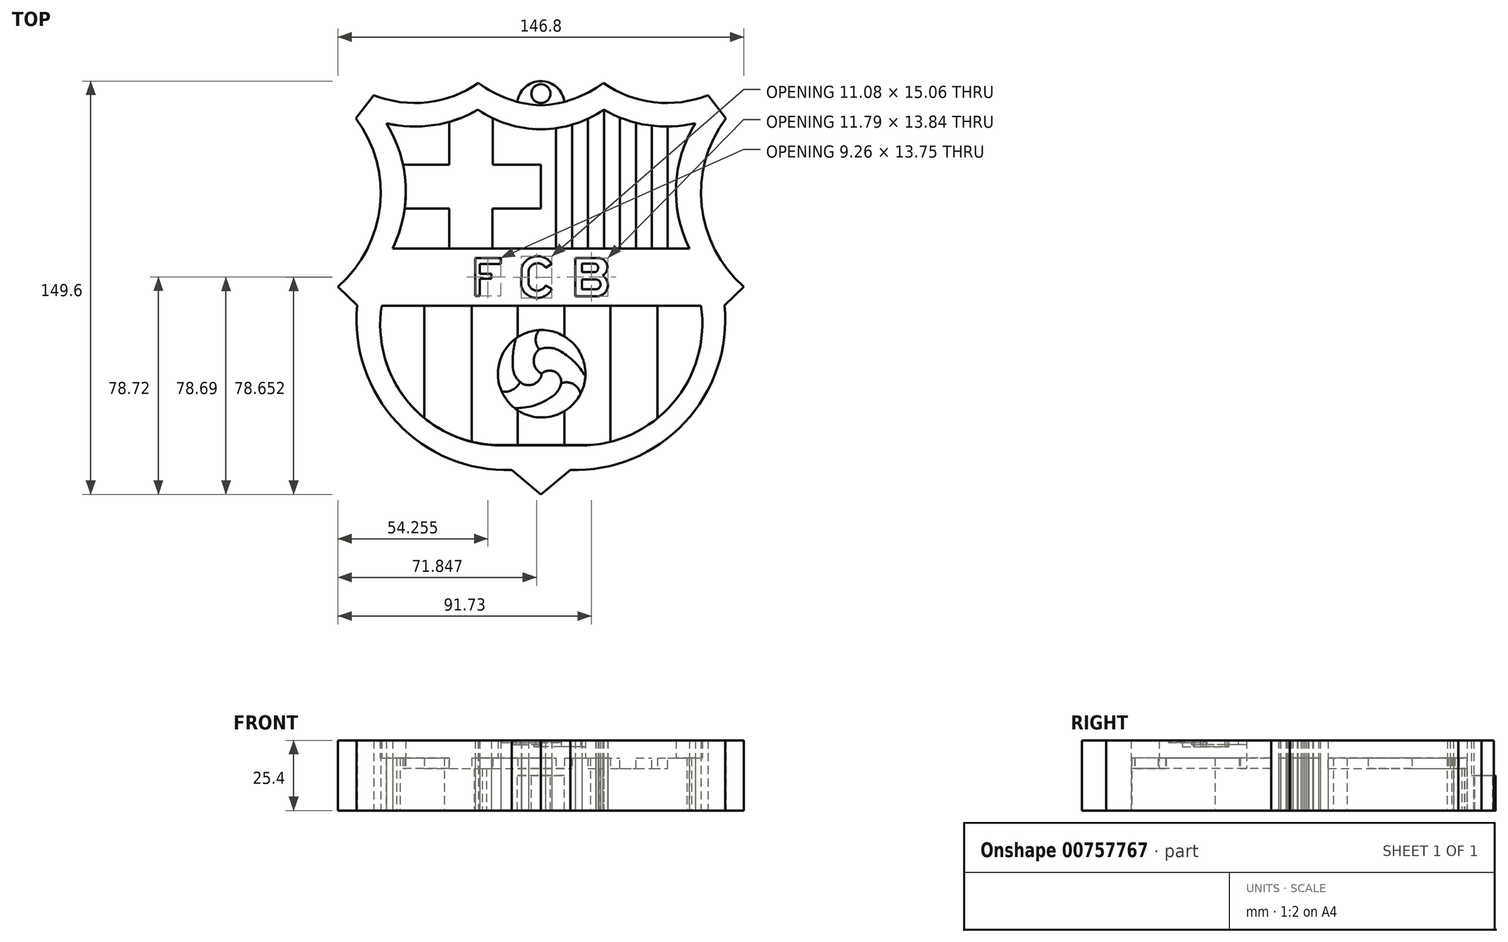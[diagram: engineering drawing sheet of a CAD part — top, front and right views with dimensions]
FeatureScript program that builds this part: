
annotation { "Feature Type Name" : "Feature", "Feature Type Description" : "" }
export const myFeature = defineFeature(function(context is Context, id is Id, definition is map)
    precondition{}
    {
        {
            var Q0;
            Q0=qCreatedBy(makeId("Top.planeOp"),FACE);
            var sketch = newSketch(context, id + "F0", { "sketchPlane" : qUnion([Q0])});
            skPoint(sketch, "E0", {"position": v(-76.27, 79.4) * mm});
            skPoint(sketch, "E1", {"position": v(76.57, -75.74) * mm});
            skLineSegment(sketch, "E2", {"start": v(-60.43, 71.38) * mm, "end": v(-66.94, 63.03) * mm});
            skLineSegment(sketch, "E3", {"start": v(-66.45, -4.73) * mm, "end": v(-73.4, 2.08) * mm});
            skArc(sketch, "E4", {"start": v(-73.4, 2.08) * mm, "mid": v(-58.2, 31.29) * mm, "end": v(-66.94, 63.03) * mm});
            skLineSegment(sketch, "E5", {"start": v(0, -73.13) * mm, "end": v(-10.6, -64.3) * mm});
            skArc(sketch, "E6", {"start": v(-66.45, -4.73) * mm, "mid": v(-51.99, -47.14) * mm, "end": v(-10.6, -64.3) * mm});
            skArc(sketch, "E7", {"start": v(-60.43, 71.38) * mm, "mid": v(-40.97, 68.83) * mm, "end": v(-22.62, 75.8) * mm});
            skArc(sketch, "E8", {"start": v(-22.62, 75.8) * mm, "mid": v(-11.9, 70.06) * mm, "end": v(0, 67.68) * mm});
            skLineSegment(sketch, "E9", {"start": v(0, 0) * mm, "end": v(0, 20) * mm, "construction": true});
            skArc(sketch, "E10.MirrorCS", {"start": v(22.62, 75.8) * mm, "mid": v(11.9, 70.06) * mm, "end": v(0, 67.68) * mm});
            skArc(sketch, "E11.MirrorCS", {"start": v(60.43, 71.38) * mm, "mid": v(40.97, 68.83) * mm, "end": v(22.62, 75.8) * mm});
            skLineSegment(sketch, "E12.MirrorCS", {"start": v(60.43, 71.38) * mm, "end": v(66.94, 63.03) * mm});
            skArc(sketch, "E13.MirrorCS", {"start": v(73.4, 2.08) * mm, "mid": v(58.2, 31.29) * mm, "end": v(66.94, 63.03) * mm});
            skLineSegment(sketch, "E14.MirrorCS", {"start": v(66.45, -4.73) * mm, "end": v(73.4, 2.08) * mm});
            skArc(sketch, "E15.MirrorCS", {"start": v(66.45, -4.73) * mm, "mid": v(51.99, -47.14) * mm, "end": v(10.6, -64.3) * mm});
            skLineSegment(sketch, "E16.MirrorCS", {"start": v(0, -73.13) * mm, "end": v(10.6, -64.3) * mm});
            skLineSegment(sketch, "E17", {"start": v(-53.66, 15.92) * mm, "end": v(0, 15.92) * mm});
            skLineSegment(sketch, "E18", {"start": v(0, 15.92) * mm, "end": v(0, 59.07) * mm});
            skArc(sketch, "E19", {"start": v(-22.73, 66.12) * mm, "mid": v(-11.89, 60.9) * mm, "end": v(0, 59.07) * mm});
            skArc(sketch, "E20", {"start": v(-55.86, 61.22) * mm, "mid": v(-38.83, 60.53) * mm, "end": v(-22.73, 66.12) * mm});
            skArc(sketch, "E21", {"start": v(-53.66, 15.92) * mm, "mid": v(-48.93, 38.85) * mm, "end": v(-55.86, 61.22) * mm});
            skLineSegment(sketch, "E22", {"start": v(0, 15.92) * mm, "end": v(53.66, 15.92) * mm});
            skArc(sketch, "E23.MirrorCS", {"start": v(22.73, 66.12) * mm, "mid": v(11.89, 60.9) * mm, "end": v(0, 59.07) * mm});
            skArc(sketch, "E24.MirrorCS", {"start": v(55.86, 61.22) * mm, "mid": v(38.83, 60.53) * mm, "end": v(22.73, 66.12) * mm});
            skArc(sketch, "E25.MirrorCS", {"start": v(53.66, 15.92) * mm, "mid": v(48.93, 38.85) * mm, "end": v(55.86, 61.22) * mm});
            skLineSegment(sketch, "E26", {"start": v(57.9, -4.76) * mm, "end": v(-57.54, -4.76) * mm});
            skCircle(sketch, "E27", {"center": v(0.28, -29.44) * mm, "radius": 15.83 * mm});
            skLineSegment(sketch, "E28", {"start": v(-14.52, -55.39) * mm, "end": v(14.4, -55.39) * mm});
            skArc(sketch, "E29", {"start": v(-57.54, -4.76) * mm, "mid": v(-47.74, -40.02) * mm, "end": v(-14.52, -55.39) * mm});
            skArc(sketch, "E30", {"start": v(14.4, -55.39) * mm, "mid": v(47.77, -40.06) * mm, "end": v(57.9, -4.76) * mm});
            skArc(sketch, "E31", {"start": v(-7.51, -32.42) * mm, "mid": v(-2.72, -33.27) * mm, "end": v(0.28, -29.44) * mm});
            skArc(sketch, "E32", {"start": v(-14.15, -35.94) * mm, "mid": v(-10.27, -35.25) * mm, "end": v(-7.51, -32.42) * mm});
            skArc(sketch, "E33", {"start": v(7.38, -32.9) * mm, "mid": v(5.02, -28.72) * mm, "end": v(0.28, -29.44) * mm});
            skArc(sketch, "E34", {"start": v(14.31, -36.77) * mm, "mid": v(11.75, -33.2) * mm, "end": v(7.38, -32.9) * mm});
            skArc(sketch, "E35", {"start": v(-0.6, -20.63) * mm, "mid": v(-2.57, -25.28) * mm, "end": v(0.28, -29.44) * mm});
            skArc(sketch, "E36", {"start": v(-0.6, -13.64) * mm, "mid": v(-1.92, -17.14) * mm, "end": v(-0.6, -20.63) * mm});
            skArc(sketch, "E37", {"start": v(-10.04, -27.9) * mm, "mid": v(-9.2, -30.4) * mm, "end": v(-7.51, -32.42) * mm});
            skArc(sketch, "E38", {"start": v(-9.08, -16.68) * mm, "mid": v(-10.07, -22.25) * mm, "end": v(-10.04, -27.9) * mm});
            skArc(sketch, "E39", {"start": v(3.53, -38.02) * mm, "mid": v(6, -35.87) * mm, "end": v(7.38, -32.9) * mm});
            skArc(sketch, "E40", {"start": v(-9.55, -41.84) * mm, "mid": v(-2.7, -41) * mm, "end": v(3.53, -38.02) * mm});
            skArc(sketch, "E41", {"start": v(7.38, -21.5) * mm, "mid": v(3.5, -20.07) * mm, "end": v(-0.6, -20.63) * mm});
            skArc(sketch, "E42", {"start": v(16.09, -30.2) * mm, "mid": v(12.26, -25.33) * mm, "end": v(7.38, -21.5) * mm});
            skLineSegment(sketch, "E43", {"start": v(-23.7, 12.46) * mm, "end": v(-14.52, 12.46) * mm});
            skLineSegment(sketch, "E44", {"start": v(-14.52, 12.46) * mm, "end": v(-14.52, 10.23) * mm});
            skLineSegment(sketch, "E45", {"start": v(-14.52, 10.23) * mm, "end": v(-22.05, 10.23) * mm});
            skLineSegment(sketch, "E46", {"start": v(-22.05, 10.23) * mm, "end": v(-22.05, 6.7) * mm});
            skLineSegment(sketch, "E47", {"start": v(-22.05, 6.7) * mm, "end": v(-17.95, 6.7) * mm});
            skLineSegment(sketch, "E48", {"start": v(-17.95, 6.7) * mm, "end": v(-17.95, 4.93) * mm});
            skLineSegment(sketch, "E49", {"start": v(-17.95, 4.93) * mm, "end": v(-22.05, 4.93) * mm});
            skLineSegment(sketch, "E50", {"start": v(-22.05, 4.93) * mm, "end": v(-22.05, -1.28) * mm});
            skLineSegment(sketch, "E51", {"start": v(-22.05, -1.28) * mm, "end": v(-23.77, -1.28) * mm});
            skLineSegment(sketch, "E52", {"start": v(-23.77, -1.28) * mm, "end": v(-23.7, 12.46) * mm});
            skArc(sketch, "E53", {"start": v(-4.47, 3.16) * mm, "mid": v(-1.6, 0.65) * mm, "end": v(1.71, 2.57) * mm});
            skArc(sketch, "E54", {"start": v(1.66, 8.95) * mm, "mid": v(-1.7, 10.52) * mm, "end": v(-4.42, 8.01) * mm});
            skArc(sketch, "E55", {"start": v(3.99, 10.24) * mm, "mid": v(-2.05, 13.05) * mm, "end": v(-7.05, 8.66) * mm});
            skArc(sketch, "E56", {"start": v(-7.1, 2.27) * mm, "mid": v(-1.88, -2) * mm, "end": v(3.99, 1.33) * mm});
            skLineSegment(sketch, "E57", {"start": v(1.66, 8.95) * mm, "end": v(3.99, 10.24) * mm});
            skLineSegment(sketch, "E58", {"start": v(1.71, 2.57) * mm, "end": v(3.99, 1.33) * mm});
            skLineSegment(sketch, "E59", {"start": v(-4.47, 3.16) * mm, "end": v(-4.42, 8.01) * mm});
            skLineSegment(sketch, "E60", {"start": v(-7.05, 8.66) * mm, "end": v(-7.1, 2.27) * mm});
            skLineSegment(sketch, "E61", {"start": v(12.43, 12.48) * mm, "end": v(12.43, -1.36) * mm});
            skLineSegment(sketch, "E62", {"start": v(12.43, -1.36) * mm, "end": v(21, -1.36) * mm});
            skLineSegment(sketch, "E63", {"start": v(12.43, 12.48) * mm, "end": v(20.7, 12.48) * mm});
            skArc(sketch, "E64", {"start": v(22.34, 6.14) * mm, "mid": v(23.97, 9.95) * mm, "end": v(20.7, 12.48) * mm});
            skArc(sketch, "E65", {"start": v(21, -1.36) * mm, "mid": v(24.2, 1.94) * mm, "end": v(22.34, 6.14) * mm});
            skLineSegment(sketch, "E66", {"start": v(14.89, 10.38) * mm, "end": v(14.89, 7.4) * mm});
            skLineSegment(sketch, "E67", {"start": v(14.89, 7.4) * mm, "end": v(19.89, 7.4) * mm});
            skLineSegment(sketch, "E68", {"start": v(14.89, 10.38) * mm, "end": v(19.8, 10.38) * mm});
            skArc(sketch, "E69", {"start": v(19.89, 7.4) * mm, "mid": v(20.7, 8.91) * mm, "end": v(19.8, 10.38) * mm});
            skLineSegment(sketch, "E70", {"start": v(14.89, 4.67) * mm, "end": v(14.89, 1.14) * mm});
            skLineSegment(sketch, "E71", {"start": v(14.89, 1.14) * mm, "end": v(19.98, 1.14) * mm});
            skLineSegment(sketch, "E72", {"start": v(14.89, 4.67) * mm, "end": v(19.84, 4.67) * mm});
            skArc(sketch, "E73", {"start": v(19.98, 1.14) * mm, "mid": v(21.6, 2.97) * mm, "end": v(19.84, 4.67) * mm});
            skLineSegment(sketch, "E74", {"start": v(0, 59.07) * mm, "end": v(0, 15.92) * mm});
            skSolve(sketch);
        }
        {
            var Q0;
            Q0=makeQuery(id+"F0.imprint","IMPRINT",FACE,{"disambiguationData":[TD([[makeQuery(id+"F0.imprint","IMPRINT",EDGE,{"derivedFrom":sQuery(id+"F0.wireOp",EDGE,"E2")}),1.0]])]});
            var Q1;
            Q1=makeQuery(id+"F0.imprint","IMPRINT",FACE,{"disambiguationData":[TD([[makeQuery(id+"F0.imprint","IMPRINT",EDGE,{"derivedFrom":sQuery(id+"F0.wireOp",EDGE,"E70")}),1.0]])]});
            var Q2;
            Q2=makeQuery(id+"F0.imprint","IMPRINT",FACE,{"disambiguationData":[TD([[makeQuery(id+"F0.imprint","IMPRINT",EDGE,{"derivedFrom":sQuery(id+"F0.wireOp",EDGE,"E66")}),1.0]])]});
            extrude(context, id + "F1", {"entities" : qUnion([Q0, Q1, Q2]), "depth" : 25.4 * mm, "offsetDistance" : 25.4 * mm});
        }
        {
            var Q0;
            Q0=qCreatedBy(makeId("Top.planeOp"),FACE);
            var sketch = newSketch(context, id + "F2", { "sketchPlane" : qUnion([Q0])});
            skLineSegment(sketch, "E75", {"start": v(0, 59.08) * mm, "end": v(0, 15.9) * mm});
            skLineSegment(sketch, "E76", {"start": v(0, 15.9) * mm, "end": v(-53.6, 15.9) * mm});
            skLineSegment(sketch, "E77", {"start": v(-53.6, 15.9) * mm, "end": v(53.65, 15.9) * mm});
            skLineSegment(sketch, "E78", {"start": v(-33.18, 15.9) * mm, "end": v(-33.18, 30.4) * mm});
            skLineSegment(sketch, "E79", {"start": v(-33.18, 30.4) * mm, "end": v(-49.25, 30.4) * mm});
            skLineSegment(sketch, "E80", {"start": v(-17.48, 15.9) * mm, "end": v(-17.48, 30.4) * mm});
            skLineSegment(sketch, "E81", {"start": v(-17.48, 30.4) * mm, "end": v(0, 30.4) * mm});
            skLineSegment(sketch, "E82", {"start": v(-17.47, 46.21) * mm, "end": v(0, 46.21) * mm});
            skLineSegment(sketch, "E83", {"start": v(-17.47, 46.21) * mm, "end": v(-17.47, 63.13) * mm});
            skLineSegment(sketch, "E84", {"start": v(-33.09, 46.2) * mm, "end": v(-33.09, 61.74) * mm});
            skLineSegment(sketch, "E85", {"start": v(-33.09, 46.2) * mm, "end": v(-49.97, 46.2) * mm});
            skArc(sketch, "E86", {"start": v(-49.25, 30.4) * mm, "mid": v(-48.9, 38.33) * mm, "end": v(-49.97, 46.2) * mm});
            skArc(sketch, "E87", {"start": v(-33.09, 61.74) * mm, "mid": v(-27.75, 63.57) * mm, "end": v(-22.75, 66.16) * mm});
            skArc(sketch, "E88", {"start": v(-22.75, 66.16) * mm, "mid": v(-20.18, 64.52) * mm, "end": v(-17.47, 63.13) * mm});
            skLineSegment(sketch, "E89", {"start": v(0, 15.9) * mm, "end": v(0, 59.08) * mm});
            skArc(sketch, "E90", {"start": v(55.86, 61.24) * mm, "mid": v(48.96, 38.85) * mm, "end": v(53.65, 15.9) * mm});
            skArc(sketch, "E91", {"start": v(22.75, 66.11) * mm, "mid": v(38.85, 60.6) * mm, "end": v(55.86, 61.24) * mm});
            skArc(sketch, "E92", {"start": v(0, 59.08) * mm, "mid": v(11.88, 60.97) * mm, "end": v(22.75, 66.11) * mm});
            skLineSegment(sketch, "E93", {"start": v(5.48, 15.9) * mm, "end": v(5.48, 59.52) * mm});
            skLineSegment(sketch, "E94", {"start": v(11.3, 15.9) * mm, "end": v(11.3, 60.8) * mm});
            skLineSegment(sketch, "E95", {"start": v(17, 15.9) * mm, "end": v(17, 62.93) * mm});
            skLineSegment(sketch, "E96", {"start": v(22.82, 15.9) * mm, "end": v(22.82, 66.07) * mm});
            skLineSegment(sketch, "E97", {"start": v(28.62, 15.9) * mm, "end": v(28.62, 63.32) * mm});
            skLineSegment(sketch, "E98", {"start": v(34.35, 15.9) * mm, "end": v(34.35, 61.48) * mm});
            skLineSegment(sketch, "E99", {"start": v(40.13, 15.9) * mm, "end": v(40.13, 60.42) * mm});
            skLineSegment(sketch, "E100", {"start": v(45.9, 15.9) * mm, "end": v(45.9, 60.1) * mm});
            skLineSegment(sketch, "E101", {"start": v(-57.54, -4.76) * mm, "end": v(57.91, -4.76) * mm});
            skLineSegment(sketch, "E102", {"start": v(-42.21, -4.76) * mm, "end": v(-42.21, -45.42) * mm});
            skLineSegment(sketch, "E103", {"start": v(-25.03, -4.76) * mm, "end": v(-25.03, -54.02) * mm});
            skLineSegment(sketch, "E104", {"start": v(-8.43, -4.76) * mm, "end": v(-8.43, -55.18) * mm});
            skLineSegment(sketch, "E105", {"start": v(8.52, -4.76) * mm, "end": v(8.52, -55.22) * mm});
            skLineSegment(sketch, "E106", {"start": v(25.2, -4.76) * mm, "end": v(25.2, -54.09) * mm});
            skLineSegment(sketch, "E107", {"start": v(42.14, -4.76) * mm, "end": v(42.14, -45.59) * mm});
            skArc(sketch, "E108", {"start": v(-57.54, -4.76) * mm, "mid": v(-48.81, -38.68) * mm, "end": v(-17.9, -55.16) * mm});
            skArc(sketch, "E109", {"start": v(18.4, -55.25) * mm, "mid": v(49.07, -38.54) * mm, "end": v(57.91, -4.76) * mm});
            skLineSegment(sketch, "E110", {"start": v(-17.9, -55.16) * mm, "end": v(18.4, -55.25) * mm});
            skArc(sketch, "E111", {"start": v(-53.6, 15.9) * mm, "mid": v(-48.99, 38.82) * mm, "end": v(-55.83, 61.17) * mm});
            skArc(sketch, "E112", {"start": v(-55.83, 61.17) * mm, "mid": v(-44.43, 60.1) * mm, "end": v(-33.09, 61.74) * mm});
            skArc(sketch, "E113", {"start": v(-17.47, 63.13) * mm, "mid": v(-8.95, 60.16) * mm, "end": v(0, 59.08) * mm});
            skSolve(sketch);
        }
        {
            var Q0;
            {var subQ0=sQuery(id+"F2.wireOp",EDGE,"E84");Q0=makeQuery(id+"F2.imprint","IMPRINT",FACE,{"disambiguationData":[TD([[makeQuery(id+"F2.imprint","IMPRINT",EDGE,{"derivedFrom":subQ0}),1.0]])]});}
            var Q1;
            {var subQ0=sQuery(id+"F2.wireOp",EDGE,"E82");Q1=makeQuery(id+"F2.imprint","IMPRINT",FACE,{"disambiguationData":[TD([[makeQuery(id+"F2.imprint","IMPRINT",EDGE,{"derivedFrom":subQ0}),1.0]])]});}
            var Q2;
            {var subQ0=sQuery(id+"F2.wireOp",EDGE,"E80");Q2=makeQuery(id+"F2.imprint","IMPRINT",FACE,{"disambiguationData":[TD([[makeQuery(id+"F2.imprint","IMPRINT",EDGE,{"derivedFrom":subQ0}),-1.0]])]});}
            var Q3;
            {var subQ4=sQuery(id+"F2.wireOp",EDGE,"E78");Q3=makeQuery(id+"F2.imprint","IMPRINT",FACE,{"disambiguationData":[TD([[makeQuery(id+"F2.imprint","IMPRINT",EDGE,{"derivedFrom":subQ4}),1.0]])]});}
            var Q4;
            {var subQ3=sQuery(id+"F2.wireOp",EDGE,"E102");Q4=makeQuery(id+"F2.imprint","IMPRINT",FACE,{"disambiguationData":[TD([[makeQuery(id+"F2.imprint","IMPRINT",EDGE,{"derivedFrom":subQ3}),-1.0]])]});}
            var Q5;
            {var subQ1=sQuery(id+"F2.wireOp",EDGE,"E103");Q5=makeQuery(id+"F2.imprint","IMPRINT",FACE,{"disambiguationData":[TD([[makeQuery(id+"F2.imprint","IMPRINT",EDGE,{"derivedFrom":subQ1}),1.0]])]});}
            var Q6;
            {var subQ4=sQuery(id+"F2.wireOp",EDGE,"E105");Q6=makeQuery(id+"F2.imprint","IMPRINT",FACE,{"disambiguationData":[TD([[makeQuery(id+"F2.imprint","IMPRINT",EDGE,{"derivedFrom":subQ4}),1.0]])]});}
            var Q7;
            {var subQ3=sQuery(id+"F2.wireOp",EDGE,"E107");Q7=makeQuery(id+"F2.imprint","IMPRINT",FACE,{"disambiguationData":[TD([[makeQuery(id+"F2.imprint","IMPRINT",EDGE,{"derivedFrom":subQ3}),1.0]])]});}
            var Q8;
            {var subQ0=sQuery(id+"F2.wireOp",EDGE,"E90");Q8=makeQuery(id+"F2.imprint","IMPRINT",FACE,{"disambiguationData":[TD([[makeQuery(id+"F2.imprint","IMPRINT",EDGE,{"derivedFrom":subQ0}),-1.0]])]});}
            var Q9;
            {var subQ0=sQuery(id+"F2.wireOp",EDGE,"E98");Q9=makeQuery(id+"F2.imprint","IMPRINT",FACE,{"disambiguationData":[TD([[makeQuery(id+"F2.imprint","IMPRINT",EDGE,{"derivedFrom":subQ0}),-1.0]])]});}
            var Q10;
            {var subQ0=sQuery(id+"F2.wireOp",EDGE,"E96");Q10=makeQuery(id+"F2.imprint","IMPRINT",FACE,{"disambiguationData":[TD([[makeQuery(id+"F2.imprint","IMPRINT",EDGE,{"derivedFrom":subQ0}),-1.0]])]});}
            var Q11;
            {var subQ0=sQuery(id+"F2.wireOp",EDGE,"E94");Q11=makeQuery(id+"F2.imprint","IMPRINT",FACE,{"disambiguationData":[TD([[makeQuery(id+"F2.imprint","IMPRINT",EDGE,{"derivedFrom":subQ0}),-1.0]])]});}
            var Q12;
            {var subQ7=sQuery(id+"F2.wireOp",EDGE,"E93");Q12=makeQuery(id+"F2.imprint","IMPRINT",FACE,{"disambiguationData":[TD([[makeQuery(id+"F2.imprint","IMPRINT",EDGE,{"derivedFrom":subQ7}),1.0]])]});}
            extrude(context, id + "F3", {"entities" : qUnion([Q0, Q1, Q2, Q3, Q4, Q5, Q6, Q7, Q8, Q9, Q10, Q11, Q12]), "operationType" : NewBodyOperationType.ADD, "depth" : 19.05 * mm, "offsetDistance" : 25.4 * mm});
        }
        {
            var Q0;
            Q0 = qSketchRegion(id + "F0", true);
            var Q1;
            {var subQ0=sQuery(id+"F0.wireOp",EDGE,"E36");Q1=makeQuery(id+"F0.imprint","IMPRINT",FACE,{"disambiguationData":[TD([[makeQuery(id+"F0.imprint","IMPRINT",EDGE,{"derivedFrom":subQ0}),1.0]])]});}
            var Q2;
            {var subQ0=sQuery(id+"F0.wireOp",EDGE,"E34");Q2=makeQuery(id+"F0.imprint","IMPRINT",FACE,{"disambiguationData":[TD([[makeQuery(id+"F0.imprint","IMPRINT",EDGE,{"derivedFrom":subQ0}),1.0]])]});}
            var Q3;
            {var subQ0=sQuery(id+"F0.wireOp",EDGE,"E32");Q3=makeQuery(id+"F0.imprint","IMPRINT",FACE,{"disambiguationData":[TD([[makeQuery(id+"F0.imprint","IMPRINT",EDGE,{"derivedFrom":subQ0}),1.0]])]});}
            extrude(context, id + "F4", {"entities" : qUnion([Q0, Q1, Q2, Q3]), "operationType" : NewBodyOperationType.ADD, "depth" : 25.4 * mm, "offsetDistance" : 25.4 * mm});
        }
        {
            var Q0;
            Q0=makeQuery(id+"F0.imprint","IMPRINT",FACE,{"disambiguationData":[TD([[makeQuery(id+"F0.imprint","IMPRINT",EDGE,{"derivedFrom":sQuery(id+"F0.wireOp",EDGE,"E31")}),1.0]])]});
            extrude(context, id + "F5", {"entities" : qUnion([Q0]), "operationType" : NewBodyOperationType.ADD, "depth" : 23.88 * mm, "offsetDistance" : 25.4 * mm});
        }
        {
            var Q0;
            Q0=makeQuery(id+"F0.imprint","IMPRINT",FACE,{"disambiguationData":[TD([[makeQuery(id+"F0.imprint","IMPRINT",EDGE,{"derivedFrom":sQuery(id+"F0.wireOp",EDGE,"E33")}),-1.0]])]});
            extrude(context, id + "F6", {"entities" : qUnion([Q0]), "operationType" : NewBodyOperationType.ADD, "depth" : 23.1 * mm, "offsetDistance" : 25.4 * mm});
        }
        {
            var Q0;
            Q0=makeQuery(id+"F0.imprint","IMPRINT",FACE,{"disambiguationData":[TD([[makeQuery(id+"F0.imprint","IMPRINT",EDGE,{"derivedFrom":sQuery(id+"F0.wireOp",EDGE,"E31")}),-1.0]])]});
            extrude(context, id + "F7", {"entities" : qUnion([Q0]), "operationType" : NewBodyOperationType.ADD, "depth" : 24.64 * mm, "offsetDistance" : 25.4 * mm});
        }
        {
            var Q0;
            {var subQ9=sQuery(id+"F2.wireOp",EDGE,"E78");Q0=makeQuery(id+"F2.imprint","IMPRINT",FACE,{"disambiguationData":[TD([[makeQuery(id+"F2.imprint","IMPRINT",EDGE,{"derivedFrom":subQ9}),-1.0]])]});}
            var Q1;
            {var subQ0=sQuery(id+"F2.wireOp",EDGE,"E93");Q1=makeQuery(id+"F2.imprint","IMPRINT",FACE,{"disambiguationData":[TD([[makeQuery(id+"F2.imprint","IMPRINT",EDGE,{"derivedFrom":subQ0}),-1.0]])]});}
            var Q2;
            {var subQ0=sQuery(id+"F2.wireOp",EDGE,"E102");Q2=makeQuery(id+"F2.imprint","IMPRINT",FACE,{"disambiguationData":[TD([[makeQuery(id+"F2.imprint","IMPRINT",EDGE,{"derivedFrom":subQ0}),1.0]])]});}
            var Q3;
            {var subQ0=sQuery(id+"F2.wireOp",EDGE,"E104");Q3=makeQuery(id+"F2.imprint","IMPRINT",FACE,{"disambiguationData":[TD([[makeQuery(id+"F2.imprint","IMPRINT",EDGE,{"derivedFrom":subQ0}),1.0]])]});}
            var Q4;
            {var subQ0=sQuery(id+"F2.wireOp",EDGE,"E106");Q4=makeQuery(id+"F2.imprint","IMPRINT",FACE,{"disambiguationData":[TD([[makeQuery(id+"F2.imprint","IMPRINT",EDGE,{"derivedFrom":subQ0}),1.0]])]});}
            var Q5;
            {var subQ3=sQuery(id+"F2.wireOp",EDGE,"E95");Q5=makeQuery(id+"F2.imprint","IMPRINT",FACE,{"disambiguationData":[TD([[makeQuery(id+"F2.imprint","IMPRINT",EDGE,{"derivedFrom":subQ3}),-1.0]])]});}
            var Q6;
            {var subQ0=sQuery(id+"F2.wireOp",EDGE,"E97");Q6=makeQuery(id+"F2.imprint","IMPRINT",FACE,{"disambiguationData":[TD([[makeQuery(id+"F2.imprint","IMPRINT",EDGE,{"derivedFrom":subQ0}),-1.0]])]});}
            var Q7;
            {var subQ0=sQuery(id+"F2.wireOp",EDGE,"E99");Q7=makeQuery(id+"F2.imprint","IMPRINT",FACE,{"disambiguationData":[TD([[makeQuery(id+"F2.imprint","IMPRINT",EDGE,{"derivedFrom":subQ0}),-1.0]])]});}
            extrude(context, id + "F8", {"entities" : qUnion([Q0, Q1, Q2, Q3, Q4, Q5, Q6, Q7]), "operationType" : NewBodyOperationType.ADD, "depth" : 15.24 * mm, "offsetDistance" : 25.4 * mm});
        }
        {
            var Q0;
            Q0=makeQuery(id+"F0.imprint","IMPRINT",FACE,{"disambiguationData":[TD([[makeQuery(id+"F0.imprint","IMPRINT",EDGE,{"derivedFrom":sQuery(id+"F0.wireOp",EDGE,"E43")}),-1.0]])]});
            var Q1;
            Q1=makeQuery(id+"F0.imprint","IMPRINT",FACE,{"disambiguationData":[TD([[makeQuery(id+"F0.imprint","IMPRINT",EDGE,{"derivedFrom":sQuery(id+"F0.wireOp",EDGE,"E53")}),-1.0]])]});
            var Q2;
            Q2=makeQuery(id+"F0.imprint","IMPRINT",FACE,{"disambiguationData":[TD([[makeQuery(id+"F0.imprint","IMPRINT",EDGE,{"derivedFrom":sQuery(id+"F0.wireOp",EDGE,"E61")}),1.0]])]});
            extrude(context, id + "F9", {"entities" : qUnion([Q0, Q1, Q2]), "depth" : 19.05 * mm, "offsetDistance" : 25.4 * mm});
        }
        {
            var Q0;
            Q0=qCreatedBy(makeId("Top.planeOp"),FACE);
            cPlane(context, id + "F10", {"entities" : qUnion([Q0]), "cplaneType" : CPlaneType.OFFSET, "offset" : 12.7 * mm, "width" : 152.4 * mm, "height" : 152.4 * mm});
        }
        {
            var Q0;
            Q0=qCreatedBy(id+"F10.planeOp",FACE);
            var sketch = newSketch(context, id + "F11", { "sketchPlane" : qUnion([Q0])});
            skCircle(sketch, "E114", {"center": v(0, 67.9) * mm, "radius": 8.56 * mm});
            skArc(sketch, "E115", {"start": v(-8.5, 68.99) * mm, "mid": v(0, 67.6) * mm, "end": v(8.5, 68.98) * mm});
            skCircle(sketch, "E116", {"center": v(0, 71.95) * mm, "radius": 3.43 * mm});
            skSolve(sketch);
        }
        {
            var Q0;
            {var subQ0=sQuery(id+"F11.wireOp",EDGE,"E115");Q0=makeQuery(id+"F11.imprint","IMPRINT",FACE,{"disambiguationData":[TD([[makeQuery(id+"F11.imprint","IMPRINT",EDGE,{"derivedFrom":subQ0}),1.0]])]});}
            extrude(context, id + "F12", {"entities" : qUnion([Q0]), "operationType" : NewBodyOperationType.ADD, "oppositeDirection" : true, "depth" : 12.7 * mm, "offsetDistance" : 25.4 * mm});
        }
    });
